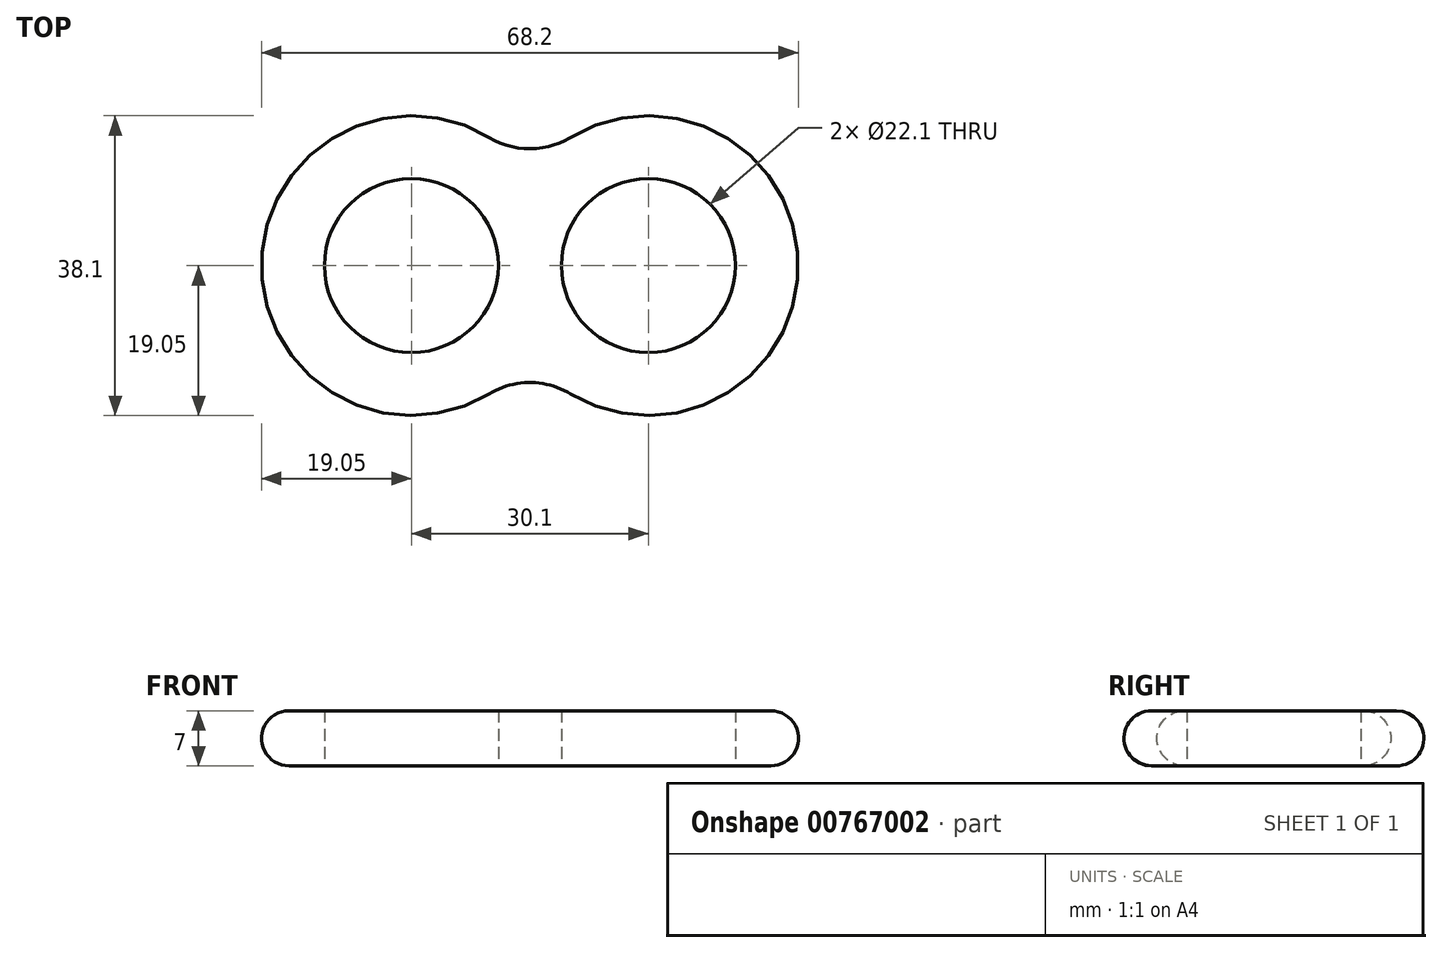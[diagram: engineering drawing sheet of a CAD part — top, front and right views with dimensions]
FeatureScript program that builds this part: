
annotation { "Feature Type Name" : "Feature", "Feature Type Description" : "" }
export const myFeature = defineFeature(function(context is Context, id is Id, definition is map)
    precondition{}
    {
        {
            var Q0;
            Q0=qCreatedBy(makeId("Top.planeOp"),FACE);
            var sketch = newSketch(context, id + "F0", { "sketchPlane" : qUnion([Q0])});
            skCircle(sketch, "E0", {"center": v(-15.05, 0) * mm, "radius": 19.05 * mm});
            skCircle(sketch, "E1", {"center": v(15.05, 0) * mm, "radius": 19.05 * mm});
            skCircle(sketch, "E2", {"center": v(15.05, 0) * mm, "radius": 11.05 * mm});
            skCircle(sketch, "E3", {"center": v(-15.05, 0) * mm, "radius": 11.05 * mm});
            skLineSegment(sketch, "E4", {"start": v(-15.05, 0) * mm, "end": v(15.05, 0) * mm, "construction": true});
            skArc(sketch, "E5", {"start": v(-5.18, 16.3) * mm, "mid": v(0, 14.85) * mm, "end": v(5.18, 16.3) * mm});
            skArc(sketch, "E6", {"start": v(5.18, -16.3) * mm, "mid": v(0, -14.85) * mm, "end": v(-5.18, -16.3) * mm});
            skSolve(sketch);
        }
        {
            var Q0;
            {var subQ5=sQuery(id+"F0.wireOp",EDGE,"E3");Q0=makeQuery(id+"F0.imprint","IMPRINT",FACE,{"disambiguationData":[TD([[makeQuery(id+"F0.imprint","IMPRINT",EDGE,{"derivedFrom":subQ5}),-1.0]])]});}
            var Q1;
            {var subQ0=sQuery(id+"F0.wireOp",EDGE,"E0");var subQ1=makeQuery(id+"F0.imprint","INTERSECT",VERTEX,{"derivedFrom":[subQ0,sQuery(id+"F0.wireOp",EDGE,"E2")]});Q1=makeQuery(id+"F0.imprint","IMPRINT",FACE,{"disambiguationData":[TD([[makeQuery(id+"F0.imprint","IMPRINT",EDGE,{"disambiguationData":[TD([[subQ1,-1.0]])],"derivedFrom":subQ0}),1.0]])]});}
            var Q2;
            {var subQ0=sQuery(id+"F0.wireOp",EDGE,"E5");Q2=makeQuery(id+"F0.imprint","IMPRINT",FACE,{"disambiguationData":[TD([[makeQuery(id+"F0.imprint","IMPRINT",EDGE,{"derivedFrom":subQ0}),-1.0]])]});}
            var Q3;
            {var subQ0=sQuery(id+"F0.wireOp",EDGE,"E6");Q3=makeQuery(id+"F0.imprint","IMPRINT",FACE,{"disambiguationData":[TD([[makeQuery(id+"F0.imprint","IMPRINT",EDGE,{"derivedFrom":subQ0}),-1.0]])]});}
            var Q4;
            {var subQ4=sQuery(id+"F0.wireOp",EDGE,"E2");Q4=makeQuery(id+"F0.imprint","IMPRINT",FACE,{"disambiguationData":[TD([[makeQuery(id+"F0.imprint","IMPRINT",EDGE,{"derivedFrom":subQ4}),-1.0]])]});}
            extrude(context, id + "F1", {"entities" : qUnion([Q0, Q1, Q2, Q3, Q4]), "depth" : 7 * mm, "offsetDistance" : 25 * mm});
        }
        {
            var Q0;
            Q0=makeQuery(id+"F1.opExtrude","CAP_EDGE",EDGE,{"disambiguationData":[OSD([sQuery(id+"F0.wireOp",EDGE,"E0")])],"isStart":false});
            var Q1;
            Q1=makeQuery(id+"F1.opExtrude","CAP_EDGE",EDGE,{"disambiguationData":[OSD([sQuery(id+"F0.wireOp",EDGE,"E0")])],"isStart":true});
            fillet(context, id + "F2", {"entities" : qUnion([Q0, Q1]), "radius" : 3.5 * mm, "tangentPropagation" : true, "allowEdgeOverflow" : false});
        }
    });
